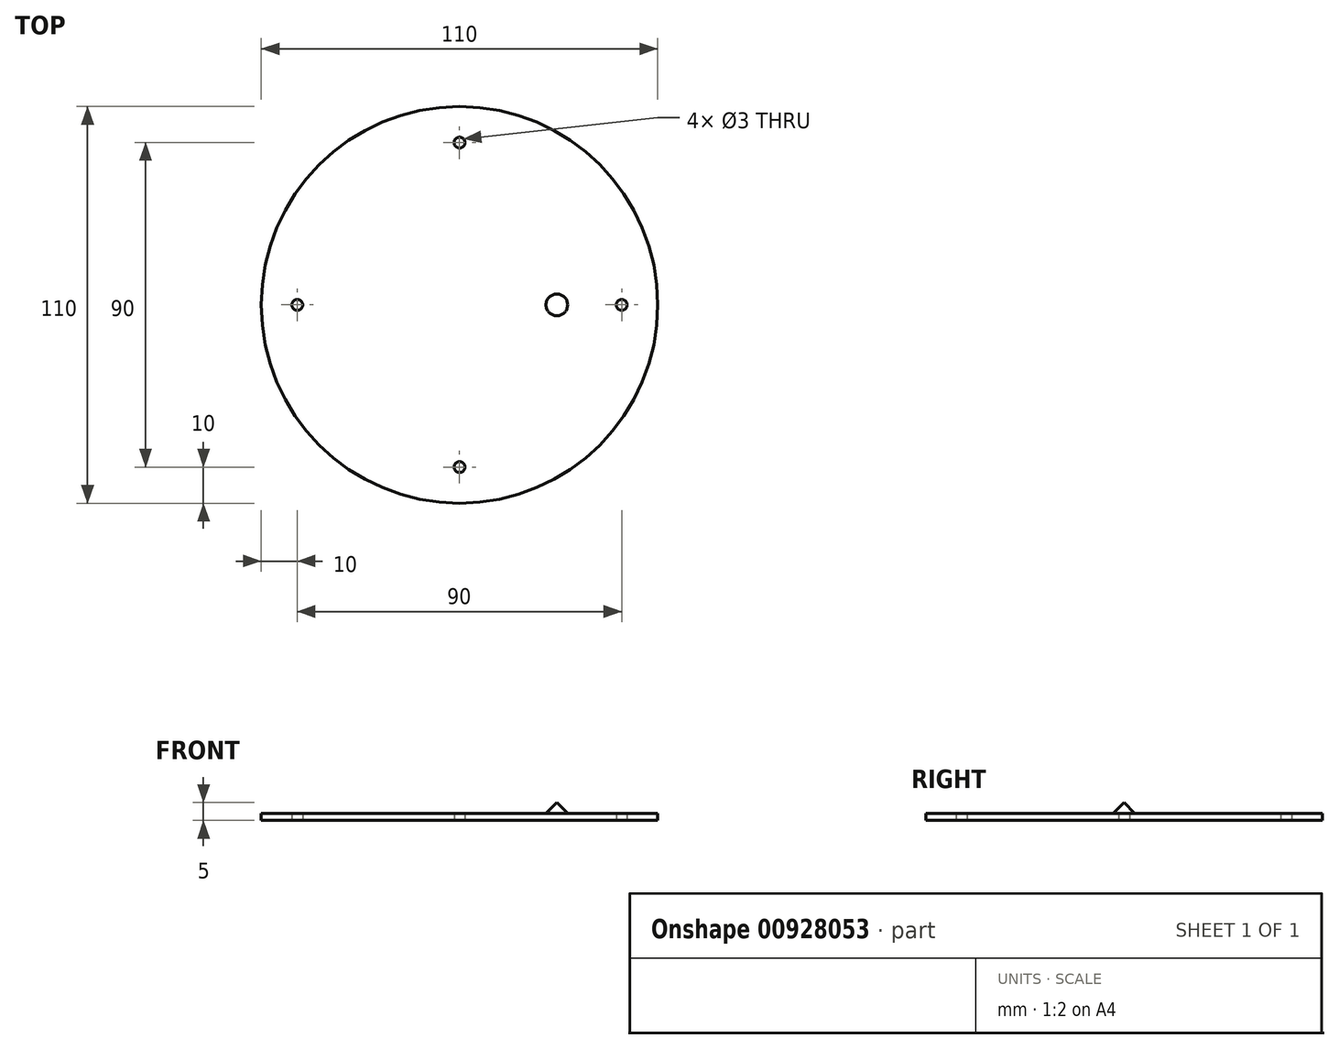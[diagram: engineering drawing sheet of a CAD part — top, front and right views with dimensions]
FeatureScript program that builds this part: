
annotation { "Feature Type Name" : "Feature", "Feature Type Description" : "" }
export const myFeature = defineFeature(function(context is Context, id is Id, definition is map)
    precondition{}
    {
        {
            var Q0;
            Q0=qCreatedBy(makeId("Top.planeOp"),FACE);
            var sketch = newSketch(context, id + "F0", { "sketchPlane" : qUnion([Q0])});
            skCircle(sketch, "E0", {"center": v(0, 0) * mm, "radius": 55 * mm});
            skSolve(sketch);
        }
        {
            var Q0;
            Q0=makeQuery(id+"F0.imprint","IMPRINT",FACE,{"disambiguationData":[TD([[makeQuery(id+"F0.imprint","IMPRINT",EDGE,{"derivedFrom":sQuery(id+"F0.wireOp",EDGE,"E0")}),1.0]])]});
            extrude(context, id + "F1", {"entities" : qUnion([Q0]), "depth" : 2 * mm, "offsetDistance" : 25 * mm});
        }
        {
            var Q0;
            Q0=makeQuery(id+"F1.opExtrude","CAP_FACE",FACE,{"disambiguationData":[OSD([sQuery(id+"F0.wireOp",EDGE,"E0")])],"isStart":true});
            var sketch = newSketch(context, id + "F2", { "sketchPlane" : qUnion([Q0])});
            skCircle(sketch, "E1", {"center": v(45, 0) * mm, "radius": 1.5 * mm});
            skCircle(sketch, "E2.1.0", {"center": v(0, 45) * mm, "radius": 1.5 * mm});
            skCircle(sketch, "E2.2.0", {"center": v(-45, 0) * mm, "radius": 1.5 * mm});
            skCircle(sketch, "E2.3.0", {"center": v(0, -45) * mm, "radius": 1.5 * mm});
            skPoint(sketch, "E2.center", {"position": v(0, 0) * mm});
            skSolve(sketch);
        }
        {
            var Q0;
            Q0=makeQuery(id+"F2.imprint","IMPRINT",FACE,{"disambiguationData":[TD([[makeQuery(id+"F2.imprint","IMPRINT",EDGE,{"derivedFrom":sQuery(id+"F2.wireOp",EDGE,"E2.2.0")}),1.0]])]});
            var Q1;
            Q1=makeQuery(id+"F2.imprint","IMPRINT",FACE,{"disambiguationData":[TD([[makeQuery(id+"F2.imprint","IMPRINT",EDGE,{"derivedFrom":sQuery(id+"F2.wireOp",EDGE,"E2.1.0")}),1.0]])]});
            var Q2;
            Q2=makeQuery(id+"F2.imprint","IMPRINT",FACE,{"disambiguationData":[TD([[makeQuery(id+"F2.imprint","IMPRINT",EDGE,{"derivedFrom":sQuery(id+"F2.wireOp",EDGE,"E1")}),1.0]])]});
            var Q3;
            Q3=makeQuery(id+"F2.imprint","IMPRINT",FACE,{"disambiguationData":[TD([[makeQuery(id+"F2.imprint","IMPRINT",EDGE,{"derivedFrom":sQuery(id+"F2.wireOp",EDGE,"E2.3.0")}),1.0]])]});
            extrude(context, id + "F3", {"entities" : qUnion([Q0, Q1, Q2, Q3]), "operationType" : NewBodyOperationType.REMOVE, "oppositeDirection" : true, "depth" : 25 * mm, "offsetDistance" : 25 * mm});
        }
        {
            var Q0;
            Q0=makeQuery(id+"F1.opExtrude","CAP_FACE",FACE,{"disambiguationData":[OSD([sQuery(id+"F0.wireOp",EDGE,"E0")])],"isStart":false});
            var sketch = newSketch(context, id + "F4", { "sketchPlane" : qUnion([Q0])});
            skCircle(sketch, "E3", {"center": v(27, 0) * mm, "radius": 5 * mm});
            skSolve(sketch);
        }
        {
            var Q0;
            Q0=makeQuery(id+"F4.imprint","IMPRINT",FACE,{"disambiguationData":[TD([[makeQuery(id+"F4.imprint","IMPRINT",EDGE,{"derivedFrom":sQuery(id+"F4.wireOp",EDGE,"6gJLyVVy-anm3-dyh3-lm5d-vpIe7ETz3JRu")}),1.0]])]});
            var Q1;
            Q1=makeQuery(id+"F4.imprint","IMPRINT",FACE,{"disambiguationData":[TD([[makeQuery(id+"F4.imprint","IMPRINT",EDGE,{"derivedFrom":sQuery(id+"F4.wireOp",EDGE,"E3")}),1.0]])]});
            extrude(context, id + "F5", {"entities" : qUnion([Q0, Q1]), "operationType" : NewBodyOperationType.ADD, "depth" : 3 * mm, "offsetDistance" : 25 * mm});
        }
        {
            var Q0;
            Q0=makeQuery(id+"F5.opExtrude","CAP_EDGE",EDGE,{"disambiguationData":[OSD([sQuery(id+"F4.wireOp",EDGE,"6gJLyVVy-anm3-dyh3-lm5d-vpIe7ETz3JRu")])],"isStart":false});
            var Q1;
            Q1=makeQuery(id+"F5.opExtrude","CAP_EDGE",EDGE,{"disambiguationData":[OSD([sQuery(id+"F4.wireOp",EDGE,"E3")])],"isStart":false});
            chamfer(context, id + "F6", {"entities" : qUnion([Q0, Q1]), "chamferType" : ChamferType.TWO_OFFSETS, "width1" : 5 * mm, "oppositeDirection" : false, "width2" : 5 * mm, "tangentPropagation" : true});
        }
    });
